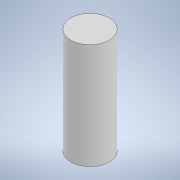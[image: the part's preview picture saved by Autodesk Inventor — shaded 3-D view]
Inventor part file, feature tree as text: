
AUTODESK INVENTOR PART (.ipt)
format: ipt  version: 2021 (Build 250183000, 183)  size: 89,088 bytes
history: native  units: mm
features: extrude x1, sketch x1
ambient origin geometry x8: Origin, YZ Plane, XZ Plane, XY Plane, X Axis, Y Axis, Z Axis, Center Point
bodies: Solid1 (feature_tree)
feature tree (2):
  extrude  "Extrusion1"  Depth=16.5mm TaperAngle=0.0deg
  sketch  "Sketch1"  dims[d0=6.0mm d1=16.5mm d2=0.0mm]
